# Revit family: OBN_End
name_source: partatom
category: Lighting Fixtures
units: mm (PartAtom-declared; Revit-internal decimal feet)

## family parameters
Cut with Voids When Loaded = No
Host = Face
Light Source = No
OmniClass Number = 23.80.70.11.21
OmniClass Title = Emergency Lighting
Part Type = Normal
Room Calculation Point = No
Round Connector Dimension = Use Diameter
Shared = No

## types (1)
- OBN
    Apparent Load = 4 VA
    Application = Healthcare Commercial, Hospitality
    Certification = CSA Listed to UL48, Standard for Electric Sign
    Default Elevation = 48.000"
    Description = The Obsidian Message Sign provides a reliable method to communicate critical messaging. The high contrast face panel clearly communicates the message in highly visible red or green letters when the sign is energized. In the Off condition, the face becomes black without any message bleed through - eliminating any confusion.
    Double Side = Yes
    End = End : C1
    Features = The LED panel is designed to provide bright and uniform illumination across the panel face
A variety of standard messages can be selected with either red or green letters. Custom messages are available upon request
Extruded aluminum body with die cast corners available in either a white or black finish
Obsidian is provided ready for surface, ceiling, end or wall-mounting with included canopy accessory, can also be recessed mounted with optional mounting kit
LED life-cycle exceeding 10 years
    Finish = White
    Glass = Glass
    Holder Material = Steel
    Lamp = LED Lamp
    Lens = Red Glass
    Load Classification = Lighting
    Manufacturer = Lifeshield
    Model = CLS
    Single Side = Yes
    Type Comments = Exit Light
    URL = https://www.currentlighting.com
    Wall Plate Material = Black
    Warranty = Fixture: 5 Years Full; Battery: 2 Years Full, 8 Years Pro-Rata
    Wattage Comments = 3.72 W
    Watts = 4 W

## geometry (parser evidence)
native form markers: Blend x4, Sweep x8
no freeform markers — native parametric forms only
